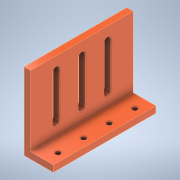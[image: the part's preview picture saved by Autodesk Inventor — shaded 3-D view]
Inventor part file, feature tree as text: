
AUTODESK INVENTOR PART (.ipt)
format: ipt  version: 2022.1 (Build 261234020, 234B)  size: 178,688 bytes
history: native  units: in
note: dims shown in document units (in); Inventor stores cm internally (conversion verified against a paired STEP export)
features: sketch x6, extrude x5, hole x1, plane x1
ambient origin geometry x8: Origin, YZ Plane, XZ Plane, XY Plane, X Axis, Y Axis, Z Axis, Center Point
bodies: Solid1 (feature_tree)
feature tree (13):
  extrude  "Extrusion1"  Depth=0.8862in
  extrude  "Extrusion2"  TaperAngle=0.0deg  [1 undecoded]
  hole  "Hole1"  [1 undecoded]
  plane  "Work Plane1"
  extrude  "Extrusion5"  Depth=0.5in
  extrude  "Extrusion6"  TaperAngle=0.0deg  [1 undecoded]
  extrude  "Extrusion7"  TaperAngle=0.0deg  [1 undecoded]
  sketch  "Sketch1"  dims[d0=4.0in d1=0.8862in]
  sketch  "Sketch2"  dims[d2=0.25in d3=0.0in]
  sketch  "Sketch4"  dims[d4=0.25in d5=3.0in]
  sketch  "Sketch7"  dims[d6=0.0in d11=0.5in]
  sketch  "Sketch8"  dims[d12=1.5748in d14=1.0in d15=0.3937in d17=1.0in]
  sketch  "Sketch9"  dims[d19=0.201in d20=0.75in d21=0.563in d22=0.12in d23=0.5635in d24=0.281in d25=0.0in d48=0.0in d49=0.0in d50=0.0in d51=3.0in d52=0.25in d53=0.0in d54=1.0in d55=0.5in d56=0.75in d58=0.266in d59=1.0in d60=0.0in d61=0.0in]
note: 4 required parameter values undecoded (feature->parameter linkage not recoverable at this tier; creation-order binding heuristic only, values carry confidence <= 0.55)
